# Revit family: BRG-SNT-LSC_LAVAMANOS OAKBROOK BLANCO
name_source: partatom
category: Aparatos sanitarios
units: mm (PartAtom-declared; Revit-internal decimal feet)

## family parameters
Compartido = Sí
Corte con vacíos al cargar = No
Cota de conector redondo = Diámetro de uso
Número OmniClass = 23.45.00.00
Punto de cálculo de habitación = Sí
Se basa en plano de trabajo = No
Siempre vertical = Sí
Tipo de pieza = Normal
Título OmniClass = Sanitary, Laundry, and Cleaning Equipment

## types (1)
- LAVAMANOS OAKBROOK
    Conexión AC = Sí
    Conexión AF = Sí
    Conexión de residuos = Sí
    Conexión de ventilación = Sí
    Elevación por defecto = 0 m
    Fabricante = BRIGGS Ecuador
    Imagen de tipo = <Ninguno>
    Modelo = LAVAMANOS OAKBROOK
    URL = https://www.briggs.com.ec
    _ALT_Basamento = 0.7 m
    _ALT_Eje instalación = 0.5 m
    _EDESA_ Alto en cm = 20.8
    _EDESA_ Ancho en cm = 52
    _EDESA_ Categoría = Productos > Sanitarios > Lavamanos > Sobre Cubierta
    _EDESA_ Certificación = Cumple con norma NTE INEN 3082
    _EDESA_ Color = blanco, bone, cherry, navy blue, verde teal, negro, cotton
    _EDESA_ Conexión Hidráulica = Entrada de agua: tubería ø 1/2" Salida de agua: tubería PVC 50
    _EDESA_ Consumo/capacidad de agua en L = 6.5 litros
    _EDESA_ Descripción = Lavamanos cubierta de mueble, instalado empotrado en mueble o mesón, con perforación para grifería monomando, 4" y 8".
    _EDESA_ Garantía = De por vida en funcionamiento y acabado de la cerámica sanitaria
    _EDESA_ Manual de instalación = https://www.briggs.com.ec
    _EDESA_ Marca = BRIGGS
    _EDESA_ Materiales = Cerámica Sanitaria
    _EDESA_ Nombre = LAVAMANOS OAKBROOK
    _EDESA_ Peso en kg = 8.0 kg
    _EDESA_ Productos necesarios para instalación = Grifería, Desagüe 1 1/4", Sifón 1 1/4", Silicón
    _EDESA_ Profundidad en cm = 44.6
    _EDESA_ Sku/código = CS0065901301CW
    _EDESA_ Tipo de instalación = Empotrado sobre cubierta de mueble
